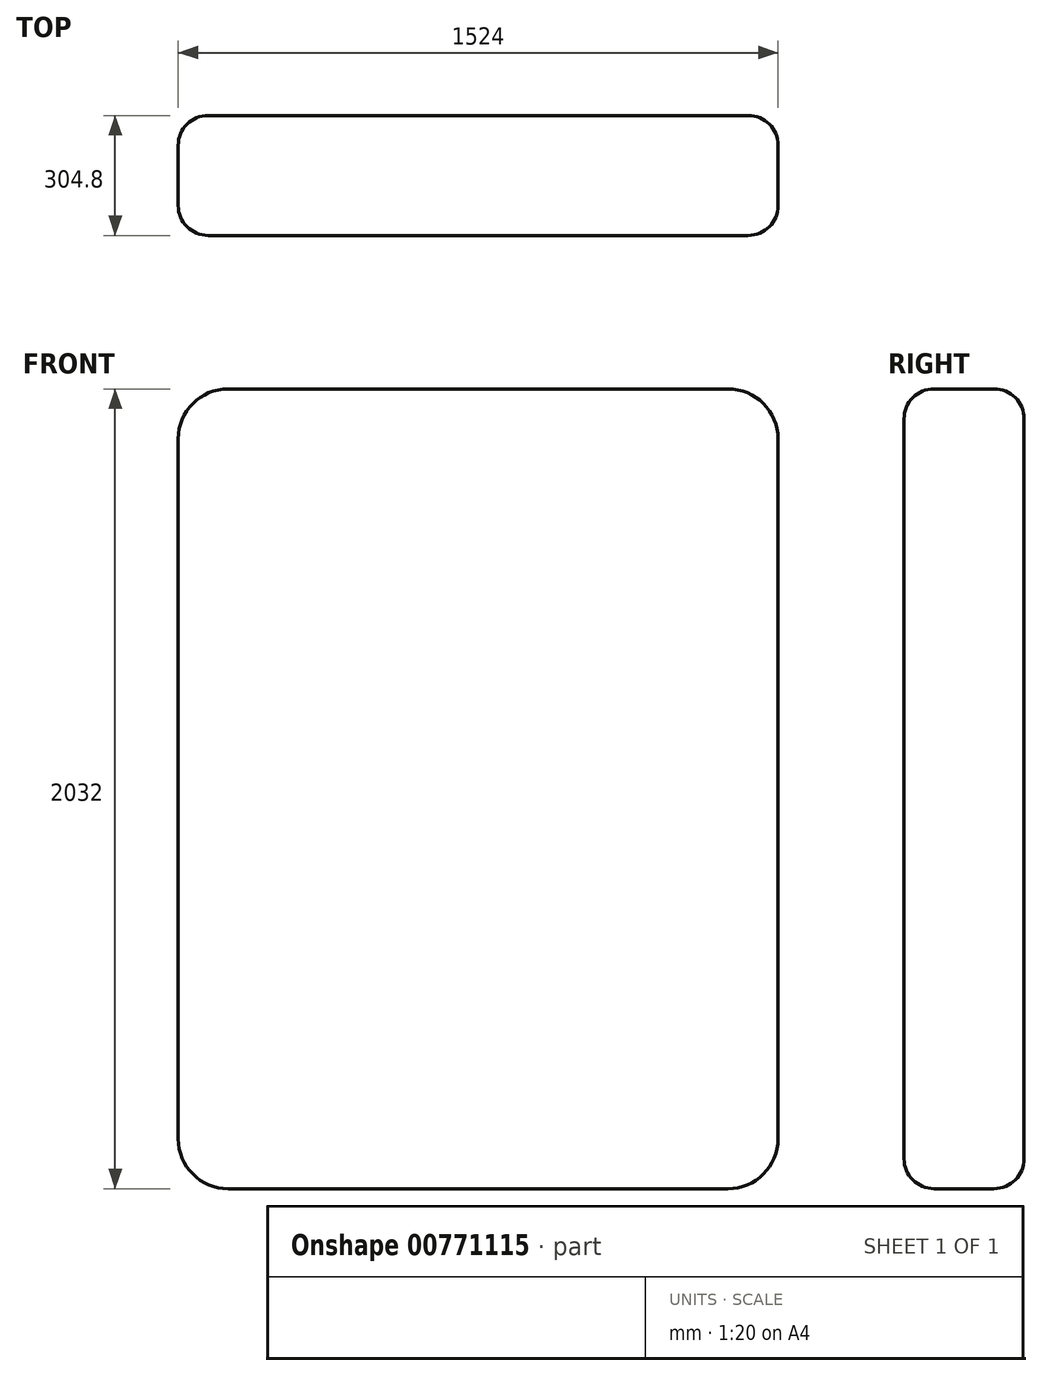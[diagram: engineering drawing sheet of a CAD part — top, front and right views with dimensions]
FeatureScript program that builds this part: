
annotation { "Feature Type Name" : "Feature", "Feature Type Description" : "" }
export const myFeature = defineFeature(function(context is Context, id is Id, definition is map)
    precondition{}
    {
        {
            var Q0;
            Q0=qCreatedBy(makeId("Front.planeOp"),FACE);
            var sketch = newSketch(context, id + "F0", { "sketchPlane" : qUnion([Q0])});
            skLineSegment(sketch, "E0.bottom", {"start": v(-762, 2032) * mm, "end": v(762, 2032) * mm});
            skLineSegment(sketch, "E0.top", {"start": v(-762, 0) * mm, "end": v(762, 0) * mm});
            skLineSegment(sketch, "E0.left", {"start": v(-762, 2032) * mm, "end": v(-762, 0) * mm});
            skLineSegment(sketch, "E0.right", {"start": v(762, 2032) * mm, "end": v(762, 0) * mm});
            skSolve(sketch);
        }
        {
            var Q0;
            Q0=makeQuery(id+"F0.imprint","IMPRINT",FACE,{"disambiguationData":[TD([[makeQuery(id+"F0.imprint","IMPRINT",EDGE,{"derivedFrom":sQuery(id+"F0.wireOp",EDGE,"E0.bottom")}),-1.0]])]});
            extrude(context, id + "F1", {"entities" : qUnion([Q0]), "depth" : 304.8 * mm, "offsetDistance" : 25.4 * mm});
        }
        {
            var Q0;
            Q0=makeQuery(id+"F1.opExtrude","SWEPT_EDGE",EDGE,{"disambiguationData":[OSD([sQuery(id+"F0.wireOp",EDGE,"E0.bottom"),sQuery(id+"F0.wireOp",EDGE,"E0.right")])]});
            var Q1;
            Q1=makeQuery(id+"F1.opExtrude","SWEPT_EDGE",EDGE,{"disambiguationData":[OSD([sQuery(id+"F0.wireOp",EDGE,"E0.bottom"),sQuery(id+"F0.wireOp",EDGE,"E0.left")])]});
            var Q2;
            Q2=makeQuery(id+"F1.opExtrude","SWEPT_EDGE",EDGE,{"disambiguationData":[OSD([sQuery(id+"F0.wireOp",EDGE,"E0.top"),sQuery(id+"F0.wireOp",EDGE,"E0.right")])]});
            var Q3;
            Q3=makeQuery(id+"F1.opExtrude","SWEPT_EDGE",EDGE,{"disambiguationData":[OSD([sQuery(id+"F0.wireOp",EDGE,"E0.top"),sQuery(id+"F0.wireOp",EDGE,"E0.left")])]});
            fillet(context, id + "F2", {"entities" : qUnion([Q0, Q1, Q2, Q3]), "radius" : 127 * mm, "tangentPropagation" : true, "allowEdgeOverflow" : false});
        }
        {
            var Q0;
            Q0=makeQuery(id+"F1.opExtrude","CAP_EDGE",EDGE,{"disambiguationData":[OSD([sQuery(id+"F0.wireOp",EDGE,"E0.left")])],"isStart":false});
            var Q1;
            Q1=makeQuery(id+"F1.opExtrude","CAP_EDGE",EDGE,{"disambiguationData":[OSD([sQuery(id+"F0.wireOp",EDGE,"E0.left")])],"isStart":true});
            fillet(context, id + "F3", {"entities" : qUnion([Q0, Q1]), "radius" : 76.2 * mm, "tangentPropagation" : true, "allowEdgeOverflow" : false});
        }
    });
